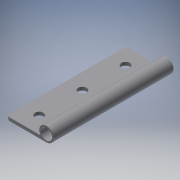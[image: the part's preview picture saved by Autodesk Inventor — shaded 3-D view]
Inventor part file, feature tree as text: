
AUTODESK INVENTOR PART (.ipt)
format: ipt  version: 2019 (Build 230136000, 136)  size: 210,432 bytes
history: native  units: mm
features: other x27, extrude x2, sketch x2, fillet x1
ambient origin geometry x8: Origin, YZ Plane, XZ Plane, XY Plane, X Axis, Y Axis, Z Axis, Center Point
bodies: Body1 (feature_tree), Body2 (feature_tree), Body3 (feature_tree)
feature tree (32):
  other  "솔리드1"
  extrude  "돌출1"  Depth=2.0mm
  fillet  "모깎기1"  Radius=2.0mm
  extrude  "돌출2"  Depth=75.0mm TaperAngle=0.0deg
  other  "작업 평면1"
  other  "작업 평면2"
  other  "작업 평면3"
  other  "작업 평면4"
  other  "작업 평면5"
  other  "분할1"
  other  "분할2"
  other  "분할3"
  other  "분할4"
  other  "분할5"
  other  "분할6"
  other  "면 삭제1"
  other  "면 삭제2"
  other  "결합1"
  sketch  "스케치1"
  sketch  "스케치2"
  other  "솔리드2"
  other  "솔리드3"
  other  "솔리드4"
  other  "솔리드5"
  other  "솔리드6"
  other  "솔리드7"
  other  "솔리드8"
  other  "솔리드9"
  other  "솔리드10"
  other  "솔리드11"
  other  "솔리드12"
  other  "솔리드13"
